# Revit family: Faucet-Wall_Mount-Lavatory-KOHLER-Avid-K-97358T_1
name_source: partatom
category: Plumbing Fixtures
revit_build: Autodesk Revit 2015 (Build: 20140606_1530(x64)
units: mm (PartAtom-declared; Revit-internal decimal feet)

## types (2) — shared parameters
ADA Compliant = No
Assembly Code = D2010
CW Connection = Yes
Cold Water Inlet = Cold Water Inlet
Date Modified = 11/07/2019
Default Elevation = 36"
Description = Wall-Mount Lavatory Faucet
Drain Included = Yes
Faucet Hole Spacing = 0"
Flow Rate = 2 GPM
HW Connection = Yes
Handle Clearance = 2 3/4"
Height = 3 13/16"
Hot Water Inlet = Hot Water Inlet
Length = 8 1/4"
Manufacturer = KOHLER Co.
MasterFormat 1995 = 15410
MasterFormat 2004 = 22.41.39
Material = Brass Construction
Pressure = 80.00 psi
Product Documentation Link = http://resources.kohler.com
Product Name = Avid
Product Page URL = https://www.kohlerasiapacific.com
Spout Reach = 8 1/4"
URL = https://www.kohlerasiapacific.com
Vent Connection = No
Waste Connection = No
Waste Water Outlet = Waste Water Outlet
WaterSense Certified = No
Width = 4"

## per-type parameters (varying)
| type | Finish | Model | Type |
| CP-Polished Chrome | Kohler-Metal-CP-Polished_Chrome | K-97358T-4-CP | 1 |
| TT-Titanium | Kohler-Metal-TT-Vibrant_Titanium | K-97358T-4-TT | 2 |

## geometry (parser evidence)
native form markers: Sweep x4
no freeform markers — native parametric forms only
